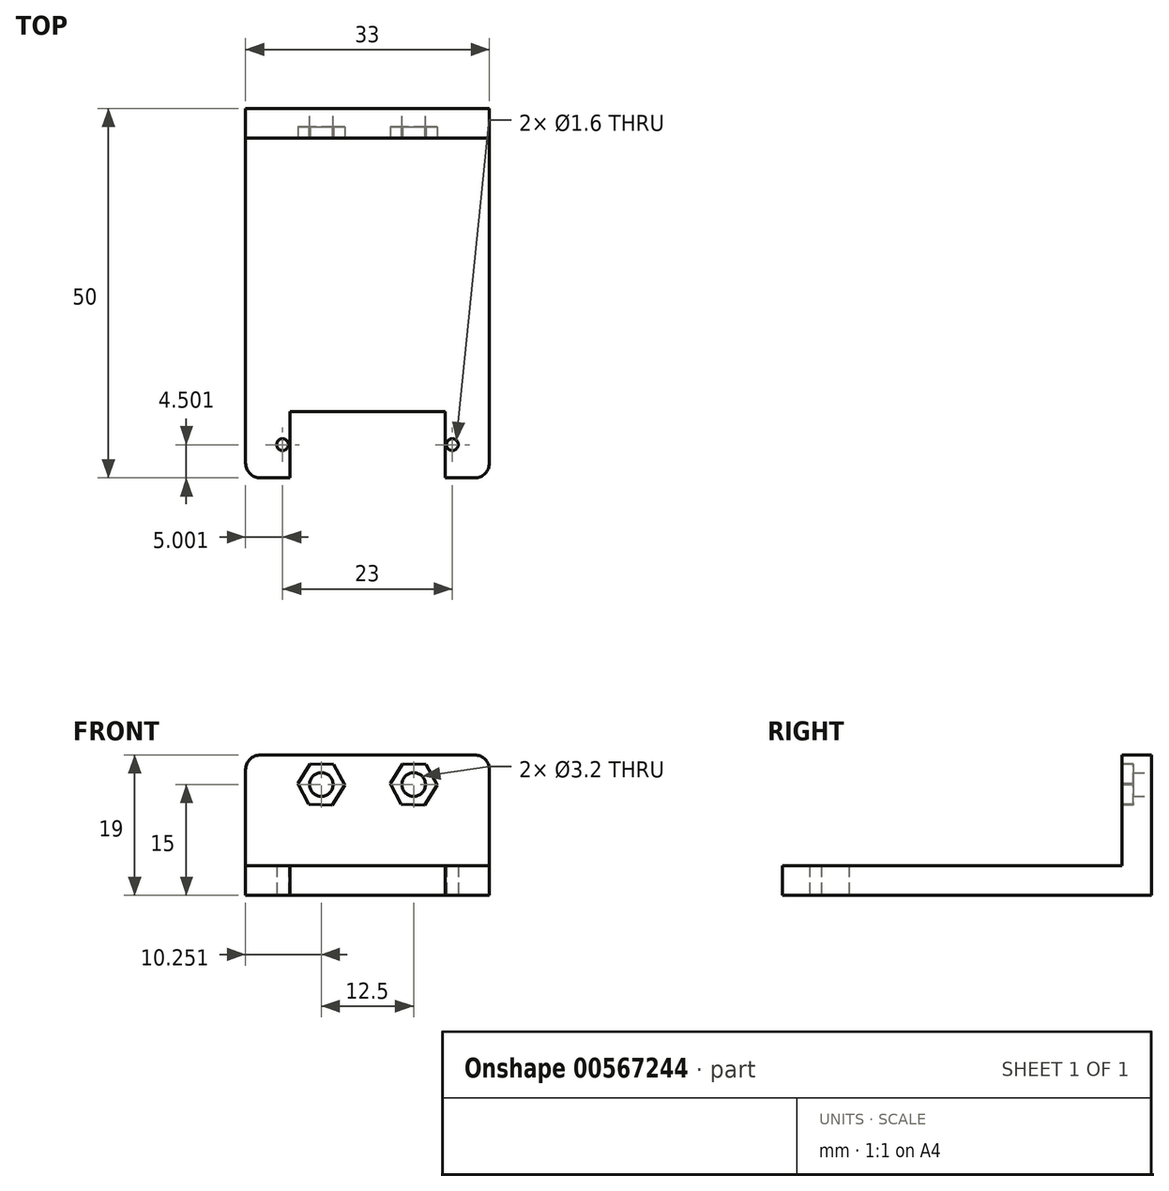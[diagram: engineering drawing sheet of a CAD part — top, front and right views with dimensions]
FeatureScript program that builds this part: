
annotation { "Feature Type Name" : "Feature", "Feature Type Description" : "" }
export const myFeature = defineFeature(function(context is Context, id is Id, definition is map)
    precondition{}
    {
        {
            var Q0;
            Q0=qCreatedBy(makeId("Top.planeOp"),FACE);
            var sketch = newSketch(context, id + "F0", { "sketchPlane" : qUnion([Q0])});
            skLineSegment(sketch, "E0.bottom", {"start": v(-44.54, 54.3) * mm, "end": v(-23.54, 54.3) * mm});
            skLineSegment(sketch, "E0.left", {"start": v(-44.54, 13.3) * mm, "end": v(-44.54, 4.3) * mm});
            skLineSegment(sketch, "E0.right", {"start": v(-23.54, 13.3) * mm, "end": v(-23.54, 4.3) * mm});
            skLineSegment(sketch, "E1.bottom", {"start": v(-50.54, 54.3) * mm, "end": v(-17.54, 54.3) * mm});
            skLineSegment(sketch, "E1.top", {"start": v(-50.54, 4.3) * mm, "end": v(-44.54, 4.3) * mm});
            skLineSegment(sketch, "E1.left", {"start": v(-50.54, 54.3) * mm, "end": v(-50.54, 4.3) * mm});
            skLineSegment(sketch, "E1.right", {"start": v(-17.54, 54.3) * mm, "end": v(-17.54, 4.3) * mm});
            skLineSegment(sketch, "E2", {"start": v(-44.54, 13.3) * mm, "end": v(-23.54, 13.3) * mm});
            skLineSegment(sketch, "E3.trimOffspring", {"start": v(-23.54, 4.3) * mm, "end": v(-17.54, 4.3) * mm});
            skCircle(sketch, "E4", {"center": v(-22.54, 8.8) * mm, "radius": 0.8 * mm});
            skPoint(sketch, "E4.centerSnap0", {"position": v(-20.54, 4.3) * mm});
            skPoint(sketch, "E4.centerSnap1", {"position": v(-23.54, 8.8) * mm});
            skCircle(sketch, "E5", {"center": v(-45.54, 8.8) * mm, "radius": 0.8 * mm});
            skPoint(sketch, "E5.centerSnap0", {"position": v(-47.54, 4.3) * mm});
            skSolve(sketch);
        }
        {
            var Q0;
            Q0=makeQuery(id+"F0.imprint","IMPRINT",FACE,{"disambiguationData":[TD([[makeQuery(id+"F0.imprint","IMPRINT",EDGE,{"derivedFrom":sQuery(id+"F0.wireOp",EDGE,"E0.left")}),-1.0]])]});
            extrude(context, id + "F1", {"entities" : qUnion([Q0]), "depth" : 4 * mm, "offsetDistance" : 25 * mm});
        }
        {
            var Q0;
            Q0=makeQuery(id+"F1.opExtrude","CAP_FACE",FACE,{"disambiguationData":[OSD([sQuery(id+"F0.wireOp",EDGE,"E0.left"),sQuery(id+"F0.wireOp",EDGE,"E0.right"),sQuery(id+"F0.wireOp",EDGE,"E1.bottom"),sQuery(id+"F0.wireOp",EDGE,"E1.top"),sQuery(id+"F0.wireOp",EDGE,"E1.left"),sQuery(id+"F0.wireOp",EDGE,"E1.right"),sQuery(id+"F0.wireOp",EDGE,"E2"),sQuery(id+"F0.wireOp",EDGE,"E3.trimOffspring"),sQuery(id+"F0.wireOp",EDGE,"E4"),sQuery(id+"F0.wireOp",EDGE,"E5")])],"isStart":false});
            var sketch = newSketch(context, id + "F2", { "sketchPlane" : qUnion([Q0])});
            skLineSegment(sketch, "E6", {"start": v(-50.54, 50.3) * mm, "end": v(-17.54, 50.3) * mm});
            skSolve(sketch);
        }
        {
            var Q0;
            {var subQ0=sQuery(id+"F2.wireOp",EDGE,"E6");Q0=makeQuery(id+"F2.imprint","IMPRINT",FACE,{"disambiguationData":[TD([[makeQuery(id+"F2.imprint","IMPRINT",EDGE,{"derivedFrom":subQ0}),1.0]])]});}
            extrude(context, id + "F3", {"entities" : qUnion([Q0]), "operationType" : NewBodyOperationType.ADD, "depth" : 15 * mm, "offsetDistance" : 25 * mm});
        }
        {
            var Q0;
            {var subQ0=sQuery(id+"F0.wireOp",EDGE,"E1.bottom");Q0=makeQuery(id+"F3.boolean.opBoolean","MERGE",FACE,{"derivedFrom":[makeQuery(id+"F1.opExtrude","SWEPT_FACE",FACE,{"disambiguationData":[OSD([subQ0])]}),makeQuery(id+"F3.opExtrude","SWEPT_FACE",FACE,{"disambiguationData":[OSD([subQ0])]})]});}
            var sketch = newSketch(context, id + "F4", { "sketchPlane" : qUnion([Q0])});
            skCircle(sketch, "E7", {"center": v(40.29, 15) * mm, "radius": 1.6 * mm});
            skCircle(sketch, "E8", {"center": v(27.79, 15) * mm, "radius": 1.6 * mm});
            skSolve(sketch);
        }
        {
            var Q0;
            Q0=makeQuery(id+"F4.imprint","IMPRINT",FACE,{"disambiguationData":[TD([[makeQuery(id+"F4.imprint","IMPRINT",EDGE,{"derivedFrom":sQuery(id+"F4.wireOp",EDGE,"E7")}),1.0]])]});
            var Q1;
            Q1=makeQuery(id+"F4.imprint","IMPRINT",FACE,{"disambiguationData":[TD([[makeQuery(id+"F4.imprint","IMPRINT",EDGE,{"derivedFrom":sQuery(id+"F4.wireOp",EDGE,"E8")}),1.0]])]});
            extrude(context, id + "F5", {"entities" : qUnion([Q0, Q1]), "operationType" : NewBodyOperationType.REMOVE, "oppositeDirection" : true, "depth" : 25 * mm, "offsetDistance" : 25 * mm});
        }
        {
            var Q0;
            Q0=makeQuery(id+"F3.opExtrude","SWEPT_FACE",FACE,{"disambiguationData":[OSD([sQuery(id+"F2.wireOp",EDGE,"E6")])]});
            var sketch = newSketch(context, id + "F6", { "sketchPlane" : qUnion([Q0])});
            skCircle(sketch, "E9.cCircle", {"center": v(-40.29, 15) * mm, "radius": 2.75 * mm, "construction": true});
            skLineSegment(sketch, "E9.0", {"start": v(-37.12, 14.9) * mm, "end": v(-38.79, 12.2) * mm});
            skLineSegment(sketch, "E9.1", {"start": v(-38.79, 12.2) * mm, "end": v(-41.96, 12.3) * mm});
            skLineSegment(sketch, "E9.2", {"start": v(-41.96, 12.3) * mm, "end": v(-43.46, 15.1) * mm});
            skLineSegment(sketch, "E9.3", {"start": v(-43.46, 15.1) * mm, "end": v(-41.79, 17.8) * mm});
            skLineSegment(sketch, "E9.4", {"start": v(-41.79, 17.8) * mm, "end": v(-38.62, 17.7) * mm});
            skLineSegment(sketch, "E9.5", {"start": v(-38.62, 17.7) * mm, "end": v(-37.12, 14.9) * mm});
            skPoint(sketch, "E9.0.midPoint", {"position": v(-37.95, 13.55) * mm});
            skCircle(sketch, "E10.cCircle", {"center": v(-27.79, 15) * mm, "radius": 2.75 * mm, "construction": true});
            skLineSegment(sketch, "E10.0", {"start": v(-24.62, 14.9) * mm, "end": v(-26.29, 12.2) * mm});
            skLineSegment(sketch, "E10.1", {"start": v(-26.29, 12.2) * mm, "end": v(-29.46, 12.3) * mm});
            skLineSegment(sketch, "E10.2", {"start": v(-29.46, 12.3) * mm, "end": v(-30.96, 15.1) * mm});
            skLineSegment(sketch, "E10.3", {"start": v(-30.96, 15.1) * mm, "end": v(-29.29, 17.8) * mm});
            skLineSegment(sketch, "E10.4", {"start": v(-29.29, 17.8) * mm, "end": v(-26.12, 17.7) * mm});
            skLineSegment(sketch, "E10.5", {"start": v(-26.12, 17.7) * mm, "end": v(-24.62, 14.9) * mm});
            skPoint(sketch, "E10.0.midPoint", {"position": v(-25.45, 13.55) * mm});
            skSolve(sketch);
        }
        {
            var Q0;
            Q0=makeQuery(id+"F6.imprint","IMPRINT",FACE,{"disambiguationData":[TD([[makeQuery(id+"F6.imprint","IMPRINT",EDGE,{"derivedFrom":sQuery(id+"F6.wireOp",EDGE,"E9.0")}),-1.0]])]});
            var Q1;
            Q1=makeQuery(id+"F6.imprint","IMPRINT",FACE,{"disambiguationData":[TD([[makeQuery(id+"F6.imprint","IMPRINT",EDGE,{"derivedFrom":sQuery(id+"F6.wireOp",EDGE,"E10.0")}),-1.0]])]});
            extrude(context, id + "F7", {"entities" : qUnion([Q0, Q1]), "operationType" : NewBodyOperationType.REMOVE, "oppositeDirection" : true, "depth" : 1.5 * mm, "offsetDistance" : 25 * mm});
        }
        {
            var Q0;
            Q0=makeQuery(id+"F1.opExtrude","SWEPT_EDGE",EDGE,{"disambiguationData":[OSD([sQuery(id+"F0.wireOp",EDGE,"E1.top"),sQuery(id+"F0.wireOp",EDGE,"E1.left")])]});
            var Q1;
            Q1=makeQuery(id+"F1.opExtrude","SWEPT_EDGE",EDGE,{"disambiguationData":[OSD([sQuery(id+"F0.wireOp",EDGE,"E1.right"),sQuery(id+"F0.wireOp",EDGE,"E3.trimOffspring")])]});
            var Q2;
            Q2=makeQuery(id+"F3.opExtrude","CAP_EDGE",EDGE,{"disambiguationData":[OSD([sQuery(id+"F0.wireOp",EDGE,"E1.right")])],"isStart":false});
            var Q3;
            Q3=makeQuery(id+"F3.opExtrude","CAP_EDGE",EDGE,{"disambiguationData":[OSD([sQuery(id+"F0.wireOp",EDGE,"E1.left")])],"isStart":false});
            var Q4;
            Q4=makeQuery(id+"F3.opExtrude","CAP_EDGE",EDGE,{"disambiguationData":[OSD([sQuery(id+"F2.wireOp",EDGE,"E6")])],"isStart":true});
            fillet(context, id + "F8", {"entities" : qUnion([Q0, Q1, Q2, Q3, Q4]), "radius" : 2 * mm, "tangentPropagation" : true, "allowEdgeOverflow" : false});
        }
    });
